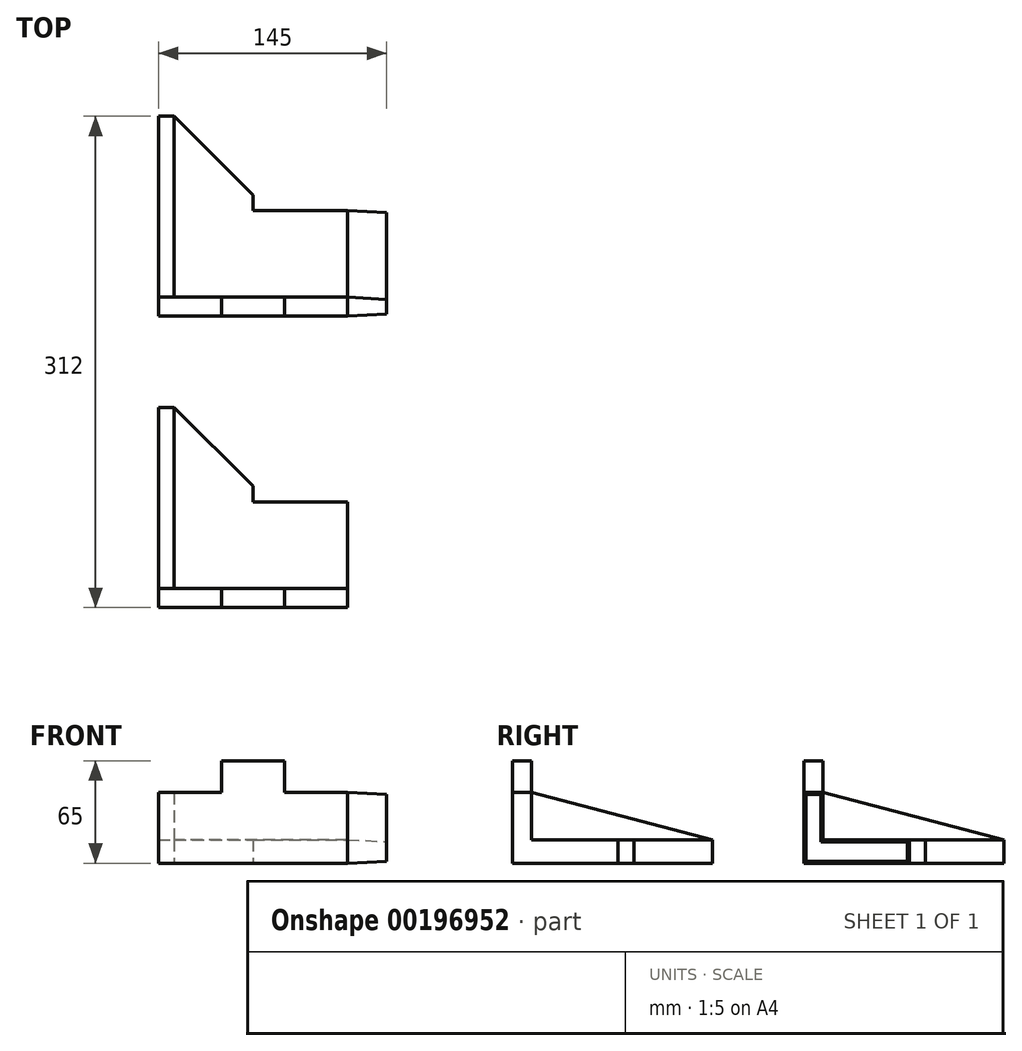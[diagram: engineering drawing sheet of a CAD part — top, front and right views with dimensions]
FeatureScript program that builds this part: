
annotation { "Feature Type Name" : "Feature", "Feature Type Description" : "" }
export const myFeature = defineFeature(function(context is Context, id is Id, definition is map)
    precondition{}
    {
        {
            var Q0;
            Q0=qCreatedBy(makeId("Front.planeOp"),FACE);
            var sketch = newSketch(context, id + "F0", { "sketchPlane" : qUnion([Q0])});
            skLineSegment(sketch, "E0", {"start": v(0, 0) * mm, "end": v(60, 0) * mm});
            skLineSegment(sketch, "E1", {"start": v(60, 0) * mm, "end": v(60, 45) * mm});
            skLineSegment(sketch, "E2", {"start": v(60, 45) * mm, "end": v(20, 45) * mm});
            skLineSegment(sketch, "E3", {"start": v(20, 45) * mm, "end": v(20, 65) * mm});
            skLineSegment(sketch, "E4", {"start": v(20, 65) * mm, "end": v(-20, 65) * mm});
            skLineSegment(sketch, "E5", {"start": v(-20, 65) * mm, "end": v(-20, 45) * mm});
            skLineSegment(sketch, "E6", {"start": v(-20, 45) * mm, "end": v(-60, 45) * mm});
            skLineSegment(sketch, "E7", {"start": v(-60, 45) * mm, "end": v(-60, 0) * mm});
            skLineSegment(sketch, "E8", {"start": v(-60, 0) * mm, "end": v(0, 0) * mm});
            skSolve(sketch);
        }
        {
            var Q0;
            Q0=qSketchRegion(id+"F0",true);
            extrude(context, id + "F1", {"entities" : qUnion([Q0]), "depth" : 12 * mm});
        }
        {
            var Q0;
            Q0=qCreatedBy(makeId("Top.planeOp"),FACE);
            var sketch = newSketch(context, id + "F2", { "sketchPlane" : qUnion([Q0])});
            skLineSegment(sketch, "E9", {"start": v(0, 0) * mm, "end": v(-60, 0) * mm});
            skLineSegment(sketch, "E10", {"start": v(-60, 0) * mm, "end": v(-60, 115) * mm});
            skLineSegment(sketch, "E11", {"start": v(-60, 115) * mm, "end": v(0, 115) * mm});
            skLineSegment(sketch, "E12", {"start": v(0, 115) * mm, "end": v(0, 55) * mm});
            skLineSegment(sketch, "E13", {"start": v(0, 55) * mm, "end": v(60, 55) * mm});
            skLineSegment(sketch, "E14", {"start": v(60, 55) * mm, "end": v(60, 0) * mm});
            skLineSegment(sketch, "E15", {"start": v(60, 0) * mm, "end": v(0, 0) * mm});
            skSolve(sketch);
        }
        {
            var Q0;
            Q0=makeQuery(id+"F2.imprint","IMPRINT",FACE,{"disambiguationData":[TD([[makeQuery(id+"F2.imprint","IMPRINT",EDGE,{"derivedFrom":sQuery(id+"F2.wireOp",EDGE,"E9")}),-1.0]])]});
            extrude(context, id + "F3", {"entities" : qUnion([Q0]), "operationType" : NewBodyOperationType.ADD, "depth" : 15 * mm});
        }
        {
            var Q0;
            Q0=makeQuery(id+"F3.boolean.opBoolean","MERGE",FACE,{"derivedFrom":[makeQuery(id+"F1.opExtrude","SWEPT_FACE",FACE,{"disambiguationData":[OSD([sQuery(id+"F0.wireOp",EDGE,"E7")])]}),makeQuery(id+"F3.opExtrude","SWEPT_FACE",FACE,{"disambiguationData":[OSD([sQuery(id+"F2.wireOp",EDGE,"E10")])]})]});
            var sketch = newSketch(context, id + "F4", { "sketchPlane" : qUnion([Q0])});
            skLineSegment(sketch, "E16", {"start": v(-115, 15) * mm, "end": v(0, 15) * mm});
            skLineSegment(sketch, "E17", {"start": v(0, 15) * mm, "end": v(0, 45) * mm});
            skLineSegment(sketch, "E18", {"start": v(0, 45) * mm, "end": v(-115, 15) * mm});
            skSolve(sketch);
        }
        {
            var Q0;
            Q0=qSketchRegion(id+"F4",true);
            extrude(context, id + "F5", {"entities" : qUnion([Q0]), "operationType" : NewBodyOperationType.ADD, "oppositeDirection" : true, "depth" : 10 * mm});
        }
        {
            var Q0;
            Q0=makeQuery(id+"F3.opExtrude","SWEPT_EDGE",EDGE,{"disambiguationData":[OSD([sQuery(id+"F2.wireOp",EDGE,"E11"),sQuery(id+"F2.wireOp",EDGE,"E12")])]});
            chamfer(context, id + "F6", {"entities" : qUnion([Q0]), "width" : 50 * mm, "tangentPropagation" : true});
        }
        {
            var Q0;
            Q0=makeQuery(id+"F1.opExtrude","SWEPT_BODY",BODY,{"disambiguationData":[OSD([sQuery(id+"F0.wireOp",EDGE,"E0"),sQuery(id+"F0.wireOp",EDGE,"E1"),sQuery(id+"F0.wireOp",EDGE,"E2"),sQuery(id+"F0.wireOp",EDGE,"E3"),sQuery(id+"F0.wireOp",EDGE,"E4"),sQuery(id+"F0.wireOp",EDGE,"E5"),sQuery(id+"F0.wireOp",EDGE,"E6"),sQuery(id+"F0.wireOp",EDGE,"E7"),sQuery(id+"F0.wireOp",EDGE,"E8")])]});
            transform(context, id + "F7", {"entities" : qUnion([Q0]), "transformType" : TransformType.TRANSLATION_3D, "dx" : 0 * mm, "dy" : 185 * mm, "dz" : 0 * mm, "makeCopy" : true});
        }
        {
            var Q0;
            Q0=makeQuery(id+"F7.opPattern","COPY",FACE,{"derivedFrom":makeQuery(id+"F3.boolean.opBoolean","MERGE",FACE,{"derivedFrom":[makeQuery(id+"F1.opExtrude","SWEPT_FACE",FACE,{"disambiguationData":[OSD([sQuery(id+"F0.wireOp",EDGE,"E1")])]}),makeQuery(id+"F3.opExtrude","SWEPT_FACE",FACE,{"disambiguationData":[OSD([sQuery(id+"F2.wireOp",EDGE,"E14")])]})]}),"instanceName":"1"});
            extrude(context, id + "F8", {"entities" : qUnion([Q0]), "operationType" : NewBodyOperationType.ADD, "depth" : 25 * mm, "hasDraft" : true, "draftAngle" : 3 * degree, "draftPullDirection" : true});
        }
    });
